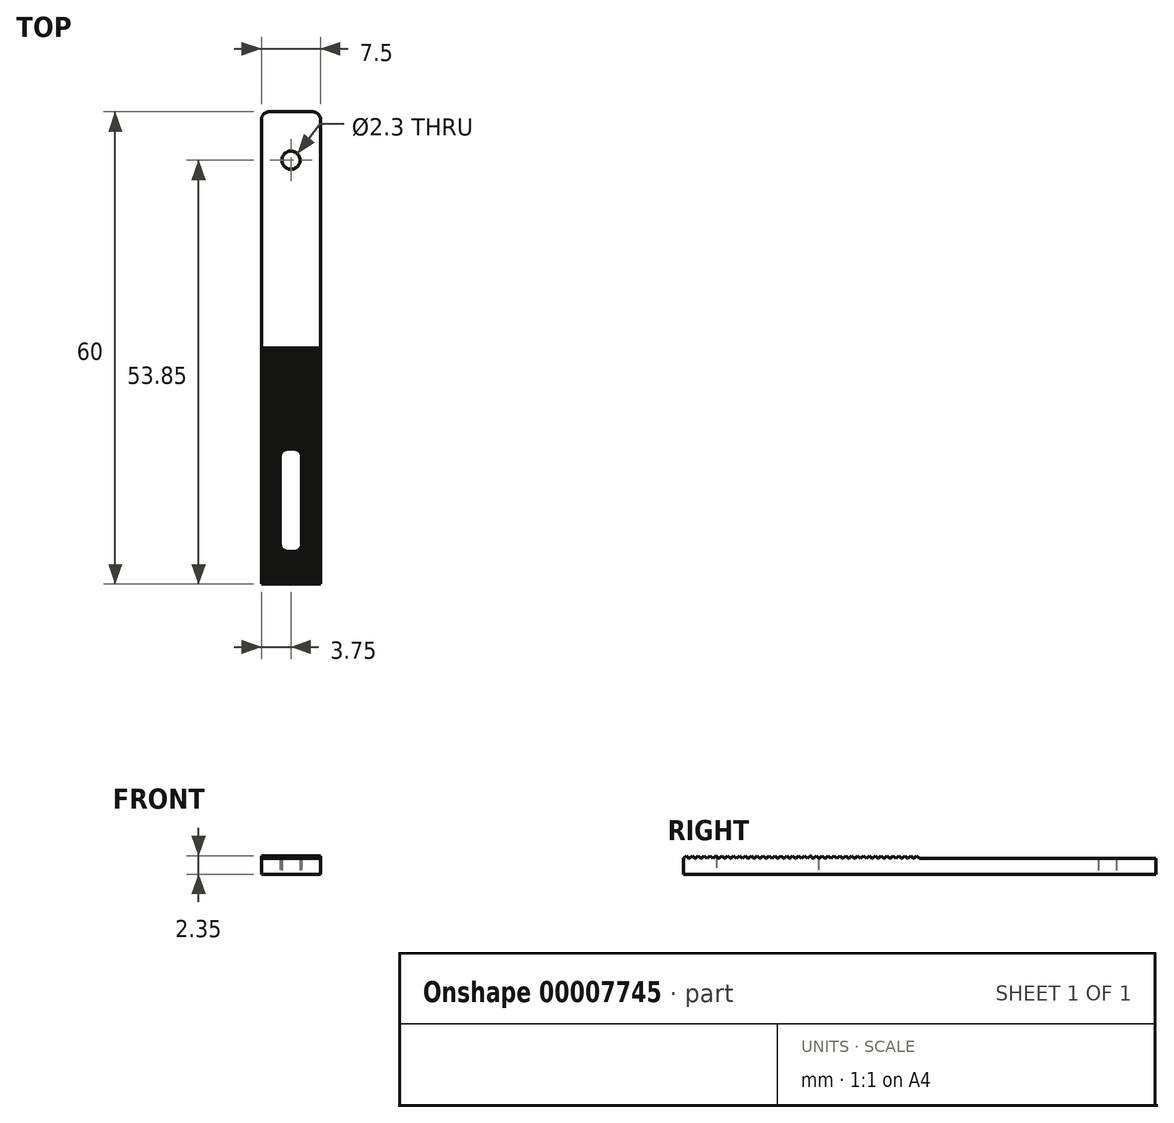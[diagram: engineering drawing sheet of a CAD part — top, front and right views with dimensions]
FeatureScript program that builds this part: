
annotation { "Feature Type Name" : "Feature", "Feature Type Description" : "" }
export const myFeature = defineFeature(function(context is Context, id is Id, definition is map)
    precondition{}
    {
        {
            var Q0;
            Q0=qCreatedBy(makeId("Top.planeOp"),FACE);
            var sketch = newSketch(context, id + "F0", { "sketchPlane" : qUnion([Q0])});
            skLineSegment(sketch, "E0.rect.bottom", {"start": v(6.5, 60) * mm, "end": v(1, 60) * mm});
            skLineSegment(sketch, "E0.rect.top", {"start": v(7.5, 0) * mm, "end": v(0, 0) * mm});
            skLineSegment(sketch, "E0.rect.left", {"start": v(7.5, 59) * mm, "end": v(7.5, 0) * mm});
            skLineSegment(sketch, "E0.rect.right", {"start": v(0, 59) * mm, "end": v(0, 0) * mm});
            skPoint(sketch, "E0.rect.middle", {"position": v(0, 0) * mm});
            skLineSegment(sketch, "E1", {"start": v(3.75, 0) * mm, "end": v(3.75, 4.15) * mm, "construction": true});
            skLineSegment(sketch, "E2.bottom", {"start": v(3.38, 4.15) * mm, "end": v(4.12, 4.15) * mm});
            skLineSegment(sketch, "E2.top", {"start": v(3.37, 17.15) * mm, "end": v(4.12, 17.15) * mm});
            skLineSegment(sketch, "E2.left", {"start": v(2.38, 5.15) * mm, "end": v(2.38, 16.15) * mm});
            skLineSegment(sketch, "E2.right", {"start": v(5.12, 5.15) * mm, "end": v(5.12, 16.15) * mm});
            skPoint(sketch, "E3.visualSharp", {"position": v(2.38, 17.15) * mm});
            skArc(sketch, "E3.filletArc", {"start": v(3.37, 17.15) * mm, "mid": v(2.67, 16.86) * mm, "end": v(2.37, 16.15) * mm});
            skPoint(sketch, "E4.visualSharp", {"position": v(5.12, 17.15) * mm});
            skArc(sketch, "E4.filletArc", {"start": v(5.12, 16.15) * mm, "mid": v(4.83, 16.86) * mm, "end": v(4.12, 17.15) * mm});
            skPoint(sketch, "E5.visualSharp", {"position": v(2.38, 4.15) * mm});
            skArc(sketch, "E5.filletArc", {"start": v(2.38, 5.15) * mm, "mid": v(2.67, 4.44) * mm, "end": v(3.38, 4.15) * mm});
            skPoint(sketch, "E6.visualSharp", {"position": v(5.12, 4.15) * mm});
            skArc(sketch, "E6.filletArc", {"start": v(4.12, 4.15) * mm, "mid": v(4.83, 4.44) * mm, "end": v(5.12, 5.15) * mm});
            skPoint(sketch, "E7.visualSharp", {"position": v(0, 60) * mm});
            skArc(sketch, "E7.filletArc", {"start": v(1, 60) * mm, "mid": v(0.3, 59.7) * mm, "end": v(0, 59) * mm});
            skPoint(sketch, "E8.visualSharp", {"position": v(7.5, 60) * mm});
            skArc(sketch, "E8.filletArc", {"start": v(7.5, 59) * mm, "mid": v(7.2, 59.7) * mm, "end": v(6.5, 60) * mm});
            skPoint(sketch, "E9", {"position": v(3.75, 60) * mm});
            skCircle(sketch, "E10", {"center": v(3.75, 53.85) * mm, "radius": 1.15 * mm});
            skLineSegment(sketch, "E11", {"start": v(3.75, 55) * mm, "end": v(3.75, 60) * mm, "construction": true});
            skSolve(sketch);
        }
        {
            var Q0;
            Q0=makeQuery(id+"F0.imprint","IMPRINT",FACE,{"disambiguationData":[TD([[makeQuery(id+"F0.imprint","IMPRINT",EDGE,{"derivedFrom":sQuery(id+"F0.wireOp",EDGE,"E0.rect.bottom")}),1.0]])]});
            extrude(context, id + "F1", {"entities" : qUnion([Q0]), "depth" : 2 * mm});
        }
        {
            var Q0;
            Q0=makeQuery(id+"F1.opExtrude","SWEPT_FACE",FACE,{"disambiguationData":[OSD([sQuery(id+"F0.wireOp",EDGE,"E0.rect.left")])]});
            var sketch = newSketch(context, id + "F2", { "sketchPlane" : qUnion([Q0])});
            skLineSegment(sketch, "E12.0", {"start": v(59, 2) * mm, "end": v(0, 2) * mm});
            skLineSegment(sketch, "E13", {"start": v(0, 2) * mm, "end": v(0.35, 2.35) * mm});
            skLineSegment(sketch, "E14", {"start": v(0.35, 2.35) * mm, "end": v(0.7, 2) * mm});
            skLineSegment(sketch, "E15.1.0.0", {"start": v(0.75, 2) * mm, "end": v(1.1, 2.35) * mm});
            skLineSegment(sketch, "E15.1.0.1", {"start": v(1.1, 2.35) * mm, "end": v(1.46, 2) * mm});
            skLineSegment(sketch, "E15.2.0.0", {"start": v(1.5, 2) * mm, "end": v(1.85, 2.35) * mm});
            skLineSegment(sketch, "E15.2.0.1", {"start": v(1.85, 2.35) * mm, "end": v(2.2, 2) * mm});
            skLineSegment(sketch, "E15.3.0.0", {"start": v(2.25, 2) * mm, "end": v(2.6, 2.35) * mm});
            skLineSegment(sketch, "E15.3.0.1", {"start": v(2.6, 2.35) * mm, "end": v(2.96, 2) * mm});
            skLineSegment(sketch, "E15.4.0.0", {"start": v(3, 2) * mm, "end": v(3.35, 2.35) * mm});
            skLineSegment(sketch, "E15.4.0.1", {"start": v(3.35, 2.35) * mm, "end": v(3.7, 2) * mm});
            skLineSegment(sketch, "E15.5.0.0", {"start": v(3.75, 2) * mm, "end": v(4.1, 2.35) * mm});
            skLineSegment(sketch, "E15.5.0.1", {"start": v(4.1, 2.35) * mm, "end": v(4.46, 2) * mm});
            skLineSegment(sketch, "E15.6.0.0", {"start": v(4.5, 2) * mm, "end": v(4.85, 2.35) * mm});
            skLineSegment(sketch, "E15.6.0.1", {"start": v(4.85, 2.35) * mm, "end": v(5.2, 2) * mm});
            skLineSegment(sketch, "E15.7.0.0", {"start": v(5.25, 2) * mm, "end": v(5.6, 2.35) * mm});
            skLineSegment(sketch, "E15.7.0.1", {"start": v(5.6, 2.35) * mm, "end": v(5.96, 2) * mm});
            skLineSegment(sketch, "E15.8.0.0", {"start": v(6, 2) * mm, "end": v(6.35, 2.35) * mm});
            skLineSegment(sketch, "E15.8.0.1", {"start": v(6.35, 2.35) * mm, "end": v(6.7, 2) * mm});
            skLineSegment(sketch, "E15.9.0.0", {"start": v(6.75, 2) * mm, "end": v(7.1, 2.35) * mm});
            skLineSegment(sketch, "E15.9.0.1", {"start": v(7.1, 2.35) * mm, "end": v(7.46, 2) * mm});
            skLineSegment(sketch, "E15.10.0.0", {"start": v(7.5, 2) * mm, "end": v(7.85, 2.35) * mm});
            skLineSegment(sketch, "E15.10.0.1", {"start": v(7.85, 2.35) * mm, "end": v(8.2, 2) * mm});
            skLineSegment(sketch, "E15.11.0.0", {"start": v(8.25, 2) * mm, "end": v(8.6, 2.35) * mm});
            skLineSegment(sketch, "E15.11.0.1", {"start": v(8.6, 2.35) * mm, "end": v(8.96, 2) * mm});
            skLineSegment(sketch, "E15.12.0.0", {"start": v(9, 2) * mm, "end": v(9.35, 2.35) * mm});
            skLineSegment(sketch, "E15.12.0.1", {"start": v(9.35, 2.35) * mm, "end": v(9.7, 2) * mm});
            skLineSegment(sketch, "E15.13.0.0", {"start": v(9.75, 2) * mm, "end": v(10.1, 2.35) * mm});
            skLineSegment(sketch, "E15.13.0.1", {"start": v(10.1, 2.35) * mm, "end": v(10.46, 2) * mm});
            skLineSegment(sketch, "E15.14.0.0", {"start": v(10.5, 2) * mm, "end": v(10.85, 2.35) * mm});
            skLineSegment(sketch, "E15.14.0.1", {"start": v(10.85, 2.35) * mm, "end": v(11.2, 2) * mm});
            skLineSegment(sketch, "E15.15.0.0", {"start": v(11.25, 2) * mm, "end": v(11.6, 2.35) * mm});
            skLineSegment(sketch, "E15.15.0.1", {"start": v(11.6, 2.35) * mm, "end": v(11.96, 2) * mm});
            skLineSegment(sketch, "E15.16.0.0", {"start": v(12, 2) * mm, "end": v(12.35, 2.35) * mm});
            skLineSegment(sketch, "E15.16.0.1", {"start": v(12.35, 2.35) * mm, "end": v(12.7, 2) * mm});
            skLineSegment(sketch, "E15.17.0.0", {"start": v(12.75, 2) * mm, "end": v(13.1, 2.35) * mm});
            skLineSegment(sketch, "E15.17.0.1", {"start": v(13.1, 2.35) * mm, "end": v(13.46, 2) * mm});
            skLineSegment(sketch, "E15.18.0.0", {"start": v(13.5, 2) * mm, "end": v(13.85, 2.35) * mm});
            skLineSegment(sketch, "E15.18.0.1", {"start": v(13.85, 2.35) * mm, "end": v(14.2, 2) * mm});
            skLineSegment(sketch, "E15.19.0.0", {"start": v(14.25, 2) * mm, "end": v(14.6, 2.35) * mm});
            skLineSegment(sketch, "E15.19.0.1", {"start": v(14.6, 2.35) * mm, "end": v(14.96, 2) * mm});
            skLineSegment(sketch, "E15.20.0.0", {"start": v(15, 2) * mm, "end": v(15.35, 2.35) * mm});
            skLineSegment(sketch, "E15.20.0.1", {"start": v(15.35, 2.35) * mm, "end": v(15.7, 2) * mm});
            skLineSegment(sketch, "E15.21.0.0", {"start": v(15.75, 2) * mm, "end": v(16.1, 2.35) * mm});
            skLineSegment(sketch, "E15.21.0.1", {"start": v(16.1, 2.35) * mm, "end": v(16.46, 2) * mm});
            skLineSegment(sketch, "E15.22.0.0", {"start": v(16.5, 2) * mm, "end": v(16.85, 2.35) * mm});
            skLineSegment(sketch, "E15.22.0.1", {"start": v(16.85, 2.35) * mm, "end": v(17.2, 2) * mm});
            skLineSegment(sketch, "E15.23.0.0", {"start": v(17.25, 2) * mm, "end": v(17.6, 2.35) * mm});
            skLineSegment(sketch, "E15.23.0.1", {"start": v(17.6, 2.35) * mm, "end": v(17.96, 2) * mm});
            skLineSegment(sketch, "E15.24.0.0", {"start": v(18, 2) * mm, "end": v(18.35, 2.35) * mm});
            skLineSegment(sketch, "E15.24.0.1", {"start": v(18.35, 2.35) * mm, "end": v(18.7, 2) * mm});
            skLineSegment(sketch, "E15.25.0.0", {"start": v(18.75, 2) * mm, "end": v(19.1, 2.35) * mm});
            skLineSegment(sketch, "E15.25.0.1", {"start": v(19.1, 2.35) * mm, "end": v(19.46, 2) * mm});
            skLineSegment(sketch, "E15.26.0.0", {"start": v(19.5, 2) * mm, "end": v(19.85, 2.35) * mm});
            skLineSegment(sketch, "E15.26.0.1", {"start": v(19.85, 2.35) * mm, "end": v(20.2, 2) * mm});
            skLineSegment(sketch, "E15.27.0.0", {"start": v(20.25, 2) * mm, "end": v(20.6, 2.35) * mm});
            skLineSegment(sketch, "E15.27.0.1", {"start": v(20.6, 2.35) * mm, "end": v(20.96, 2) * mm});
            skLineSegment(sketch, "E15.28.0.0", {"start": v(21, 2) * mm, "end": v(21.35, 2.35) * mm});
            skLineSegment(sketch, "E15.28.0.1", {"start": v(21.35, 2.35) * mm, "end": v(21.7, 2) * mm});
            skLineSegment(sketch, "E15.29.0.0", {"start": v(21.75, 2) * mm, "end": v(22.1, 2.35) * mm});
            skLineSegment(sketch, "E15.29.0.1", {"start": v(22.1, 2.35) * mm, "end": v(22.46, 2) * mm});
            skLineSegment(sketch, "E15.30.0.0", {"start": v(22.5, 2) * mm, "end": v(22.85, 2.35) * mm});
            skLineSegment(sketch, "E15.30.0.1", {"start": v(22.85, 2.35) * mm, "end": v(23.2, 2) * mm});
            skLineSegment(sketch, "E15.31.0.0", {"start": v(23.25, 2) * mm, "end": v(23.6, 2.35) * mm});
            skLineSegment(sketch, "E15.31.0.1", {"start": v(23.6, 2.35) * mm, "end": v(23.96, 2) * mm});
            skLineSegment(sketch, "E15.32.0.0", {"start": v(24, 2) * mm, "end": v(24.35, 2.35) * mm});
            skLineSegment(sketch, "E15.32.0.1", {"start": v(24.35, 2.35) * mm, "end": v(24.7, 2) * mm});
            skLineSegment(sketch, "E15.33.0.0", {"start": v(24.75, 2) * mm, "end": v(25.1, 2.35) * mm});
            skLineSegment(sketch, "E15.33.0.1", {"start": v(25.1, 2.35) * mm, "end": v(25.46, 2) * mm});
            skLineSegment(sketch, "E15.direction1", {"start": v(0, 2) * mm, "end": v(0.75, 2) * mm, "construction": true});
            skLineSegment(sketch, "E16.0.34.0", {"start": v(25.5, 2) * mm, "end": v(25.85, 2.35) * mm});
            skLineSegment(sketch, "E16.3.34.0", {"start": v(25.85, 2.35) * mm, "end": v(26.2, 2) * mm});
            skLineSegment(sketch, "E16.0.35.0", {"start": v(26.25, 2) * mm, "end": v(26.6, 2.35) * mm});
            skLineSegment(sketch, "E16.3.35.0", {"start": v(26.6, 2.35) * mm, "end": v(26.96, 2) * mm});
            skLineSegment(sketch, "E16.0.36.0", {"start": v(27, 2) * mm, "end": v(27.35, 2.35) * mm});
            skLineSegment(sketch, "E16.3.36.0", {"start": v(27.35, 2.35) * mm, "end": v(27.7, 2) * mm});
            skLineSegment(sketch, "E16.0.37.0", {"start": v(27.75, 2) * mm, "end": v(28.1, 2.35) * mm});
            skLineSegment(sketch, "E16.3.37.0", {"start": v(28.1, 2.35) * mm, "end": v(28.46, 2) * mm});
            skLineSegment(sketch, "E16.0.38.0", {"start": v(28.5, 2) * mm, "end": v(28.85, 2.35) * mm});
            skLineSegment(sketch, "E16.3.38.0", {"start": v(28.85, 2.35) * mm, "end": v(29.2, 2) * mm});
            skLineSegment(sketch, "E16.0.39.0", {"start": v(29.25, 2) * mm, "end": v(29.6, 2.35) * mm});
            skLineSegment(sketch, "E16.3.39.0", {"start": v(29.6, 2.35) * mm, "end": v(29.96, 2) * mm});
            skSolve(sketch);
        }
        {
            var Q0;
            {var subQ1=sQuery(id+"F2.wireOp",EDGE,"E16.0.39.0");Q0=makeQuery(id+"F2.imprint","IMPRINT",FACE,{"disambiguationData":[TD([[makeQuery(id+"F2.imprint","IMPRINT",EDGE,{"derivedFrom":subQ1}),-1.0]])]});}
            var Q1;
            {var subQ1=sQuery(id+"F2.wireOp",EDGE,"E16.0.38.0");Q1=makeQuery(id+"F2.imprint","IMPRINT",FACE,{"disambiguationData":[TD([[makeQuery(id+"F2.imprint","IMPRINT",EDGE,{"derivedFrom":subQ1}),-1.0]])]});}
            var Q2;
            {var subQ1=sQuery(id+"F2.wireOp",EDGE,"E16.0.37.0");Q2=makeQuery(id+"F2.imprint","IMPRINT",FACE,{"disambiguationData":[TD([[makeQuery(id+"F2.imprint","IMPRINT",EDGE,{"derivedFrom":subQ1}),-1.0]])]});}
            var Q3;
            {var subQ1=sQuery(id+"F2.wireOp",EDGE,"E16.0.36.0");Q3=makeQuery(id+"F2.imprint","IMPRINT",FACE,{"disambiguationData":[TD([[makeQuery(id+"F2.imprint","IMPRINT",EDGE,{"derivedFrom":subQ1}),-1.0]])]});}
            var Q4;
            {var subQ1=sQuery(id+"F2.wireOp",EDGE,"E16.0.35.0");Q4=makeQuery(id+"F2.imprint","IMPRINT",FACE,{"disambiguationData":[TD([[makeQuery(id+"F2.imprint","IMPRINT",EDGE,{"derivedFrom":subQ1}),-1.0]])]});}
            var Q5;
            {var subQ1=sQuery(id+"F2.wireOp",EDGE,"E16.0.34.0");Q5=makeQuery(id+"F2.imprint","IMPRINT",FACE,{"disambiguationData":[TD([[makeQuery(id+"F2.imprint","IMPRINT",EDGE,{"derivedFrom":subQ1}),-1.0]])]});}
            var Q6;
            {var subQ1=sQuery(id+"F2.wireOp",EDGE,"E15.33.0.0");Q6=makeQuery(id+"F2.imprint","IMPRINT",FACE,{"disambiguationData":[TD([[makeQuery(id+"F2.imprint","IMPRINT",EDGE,{"derivedFrom":subQ1}),-1.0]])]});}
            var Q7;
            {var subQ1=sQuery(id+"F2.wireOp",EDGE,"E15.32.0.0");Q7=makeQuery(id+"F2.imprint","IMPRINT",FACE,{"disambiguationData":[TD([[makeQuery(id+"F2.imprint","IMPRINT",EDGE,{"derivedFrom":subQ1}),-1.0]])]});}
            var Q8;
            {var subQ1=sQuery(id+"F2.wireOp",EDGE,"E15.31.0.0");Q8=makeQuery(id+"F2.imprint","IMPRINT",FACE,{"disambiguationData":[TD([[makeQuery(id+"F2.imprint","IMPRINT",EDGE,{"derivedFrom":subQ1}),-1.0]])]});}
            var Q9;
            {var subQ1=sQuery(id+"F2.wireOp",EDGE,"E15.30.0.0");Q9=makeQuery(id+"F2.imprint","IMPRINT",FACE,{"disambiguationData":[TD([[makeQuery(id+"F2.imprint","IMPRINT",EDGE,{"derivedFrom":subQ1}),-1.0]])]});}
            var Q10;
            {var subQ1=sQuery(id+"F2.wireOp",EDGE,"E15.29.0.0");Q10=makeQuery(id+"F2.imprint","IMPRINT",FACE,{"disambiguationData":[TD([[makeQuery(id+"F2.imprint","IMPRINT",EDGE,{"derivedFrom":subQ1}),-1.0]])]});}
            var Q11;
            {var subQ1=sQuery(id+"F2.wireOp",EDGE,"E15.28.0.0");Q11=makeQuery(id+"F2.imprint","IMPRINT",FACE,{"disambiguationData":[TD([[makeQuery(id+"F2.imprint","IMPRINT",EDGE,{"derivedFrom":subQ1}),-1.0]])]});}
            var Q12;
            {var subQ1=sQuery(id+"F2.wireOp",EDGE,"E15.27.0.0");Q12=makeQuery(id+"F2.imprint","IMPRINT",FACE,{"disambiguationData":[TD([[makeQuery(id+"F2.imprint","IMPRINT",EDGE,{"derivedFrom":subQ1}),-1.0]])]});}
            var Q13;
            {var subQ1=sQuery(id+"F2.wireOp",EDGE,"E15.26.0.0");Q13=makeQuery(id+"F2.imprint","IMPRINT",FACE,{"disambiguationData":[TD([[makeQuery(id+"F2.imprint","IMPRINT",EDGE,{"derivedFrom":subQ1}),-1.0]])]});}
            var Q14;
            {var subQ1=sQuery(id+"F2.wireOp",EDGE,"E15.25.0.0");Q14=makeQuery(id+"F2.imprint","IMPRINT",FACE,{"disambiguationData":[TD([[makeQuery(id+"F2.imprint","IMPRINT",EDGE,{"derivedFrom":subQ1}),-1.0]])]});}
            var Q15;
            {var subQ1=sQuery(id+"F2.wireOp",EDGE,"E15.24.0.0");Q15=makeQuery(id+"F2.imprint","IMPRINT",FACE,{"disambiguationData":[TD([[makeQuery(id+"F2.imprint","IMPRINT",EDGE,{"derivedFrom":subQ1}),-1.0]])]});}
            var Q16;
            {var subQ1=sQuery(id+"F2.wireOp",EDGE,"E15.23.0.0");Q16=makeQuery(id+"F2.imprint","IMPRINT",FACE,{"disambiguationData":[TD([[makeQuery(id+"F2.imprint","IMPRINT",EDGE,{"derivedFrom":subQ1}),-1.0]])]});}
            var Q17;
            {var subQ1=sQuery(id+"F2.wireOp",EDGE,"E15.22.0.0");Q17=makeQuery(id+"F2.imprint","IMPRINT",FACE,{"disambiguationData":[TD([[makeQuery(id+"F2.imprint","IMPRINT",EDGE,{"derivedFrom":subQ1}),-1.0]])]});}
            var Q18;
            {var subQ1=sQuery(id+"F2.wireOp",EDGE,"E15.21.0.0");Q18=makeQuery(id+"F2.imprint","IMPRINT",FACE,{"disambiguationData":[TD([[makeQuery(id+"F2.imprint","IMPRINT",EDGE,{"derivedFrom":subQ1}),-1.0]])]});}
            var Q19;
            {var subQ1=sQuery(id+"F2.wireOp",EDGE,"E15.20.0.0");Q19=makeQuery(id+"F2.imprint","IMPRINT",FACE,{"disambiguationData":[TD([[makeQuery(id+"F2.imprint","IMPRINT",EDGE,{"derivedFrom":subQ1}),-1.0]])]});}
            var Q20;
            {var subQ1=sQuery(id+"F2.wireOp",EDGE,"E15.19.0.0");Q20=makeQuery(id+"F2.imprint","IMPRINT",FACE,{"disambiguationData":[TD([[makeQuery(id+"F2.imprint","IMPRINT",EDGE,{"derivedFrom":subQ1}),-1.0]])]});}
            var Q21;
            {var subQ1=sQuery(id+"F2.wireOp",EDGE,"E15.18.0.0");Q21=makeQuery(id+"F2.imprint","IMPRINT",FACE,{"disambiguationData":[TD([[makeQuery(id+"F2.imprint","IMPRINT",EDGE,{"derivedFrom":subQ1}),-1.0]])]});}
            var Q22;
            {var subQ1=sQuery(id+"F2.wireOp",EDGE,"E15.17.0.0");Q22=makeQuery(id+"F2.imprint","IMPRINT",FACE,{"disambiguationData":[TD([[makeQuery(id+"F2.imprint","IMPRINT",EDGE,{"derivedFrom":subQ1}),-1.0]])]});}
            var Q23;
            {var subQ1=sQuery(id+"F2.wireOp",EDGE,"E15.16.0.0");Q23=makeQuery(id+"F2.imprint","IMPRINT",FACE,{"disambiguationData":[TD([[makeQuery(id+"F2.imprint","IMPRINT",EDGE,{"derivedFrom":subQ1}),-1.0]])]});}
            var Q24;
            {var subQ1=sQuery(id+"F2.wireOp",EDGE,"E15.15.0.0");Q24=makeQuery(id+"F2.imprint","IMPRINT",FACE,{"disambiguationData":[TD([[makeQuery(id+"F2.imprint","IMPRINT",EDGE,{"derivedFrom":subQ1}),-1.0]])]});}
            var Q25;
            {var subQ1=sQuery(id+"F2.wireOp",EDGE,"E15.14.0.0");Q25=makeQuery(id+"F2.imprint","IMPRINT",FACE,{"disambiguationData":[TD([[makeQuery(id+"F2.imprint","IMPRINT",EDGE,{"derivedFrom":subQ1}),-1.0]])]});}
            var Q26;
            {var subQ1=sQuery(id+"F2.wireOp",EDGE,"E15.13.0.0");Q26=makeQuery(id+"F2.imprint","IMPRINT",FACE,{"disambiguationData":[TD([[makeQuery(id+"F2.imprint","IMPRINT",EDGE,{"derivedFrom":subQ1}),-1.0]])]});}
            var Q27;
            {var subQ1=sQuery(id+"F2.wireOp",EDGE,"E15.12.0.0");Q27=makeQuery(id+"F2.imprint","IMPRINT",FACE,{"disambiguationData":[TD([[makeQuery(id+"F2.imprint","IMPRINT",EDGE,{"derivedFrom":subQ1}),-1.0]])]});}
            var Q28;
            {var subQ1=sQuery(id+"F2.wireOp",EDGE,"E15.11.0.0");Q28=makeQuery(id+"F2.imprint","IMPRINT",FACE,{"disambiguationData":[TD([[makeQuery(id+"F2.imprint","IMPRINT",EDGE,{"derivedFrom":subQ1}),-1.0]])]});}
            var Q29;
            {var subQ0=sQuery(id+"F2.wireOp",EDGE,"E15.10.0.0");Q29=makeQuery(id+"F2.imprint","IMPRINT",FACE,{"disambiguationData":[TD([[makeQuery(id+"F2.imprint","IMPRINT",EDGE,{"derivedFrom":subQ0}),-1.0]])]});}
            var Q30;
            {var subQ1=sQuery(id+"F2.wireOp",EDGE,"E15.9.0.0");Q30=makeQuery(id+"F2.imprint","IMPRINT",FACE,{"disambiguationData":[TD([[makeQuery(id+"F2.imprint","IMPRINT",EDGE,{"derivedFrom":subQ1}),-1.0]])]});}
            var Q31;
            {var subQ1=sQuery(id+"F2.wireOp",EDGE,"E15.8.0.0");Q31=makeQuery(id+"F2.imprint","IMPRINT",FACE,{"disambiguationData":[TD([[makeQuery(id+"F2.imprint","IMPRINT",EDGE,{"derivedFrom":subQ1}),-1.0]])]});}
            var Q32;
            {var subQ1=sQuery(id+"F2.wireOp",EDGE,"E15.7.0.0");Q32=makeQuery(id+"F2.imprint","IMPRINT",FACE,{"disambiguationData":[TD([[makeQuery(id+"F2.imprint","IMPRINT",EDGE,{"derivedFrom":subQ1}),-1.0]])]});}
            var Q33;
            {var subQ1=sQuery(id+"F2.wireOp",EDGE,"E15.6.0.0");Q33=makeQuery(id+"F2.imprint","IMPRINT",FACE,{"disambiguationData":[TD([[makeQuery(id+"F2.imprint","IMPRINT",EDGE,{"derivedFrom":subQ1}),-1.0]])]});}
            var Q34;
            {var subQ1=sQuery(id+"F2.wireOp",EDGE,"E15.5.0.0");Q34=makeQuery(id+"F2.imprint","IMPRINT",FACE,{"disambiguationData":[TD([[makeQuery(id+"F2.imprint","IMPRINT",EDGE,{"derivedFrom":subQ1}),-1.0]])]});}
            var Q35;
            {var subQ1=sQuery(id+"F2.wireOp",EDGE,"E15.4.0.0");Q35=makeQuery(id+"F2.imprint","IMPRINT",FACE,{"disambiguationData":[TD([[makeQuery(id+"F2.imprint","IMPRINT",EDGE,{"derivedFrom":subQ1}),-1.0]])]});}
            var Q36;
            {var subQ1=sQuery(id+"F2.wireOp",EDGE,"E15.3.0.0");Q36=makeQuery(id+"F2.imprint","IMPRINT",FACE,{"disambiguationData":[TD([[makeQuery(id+"F2.imprint","IMPRINT",EDGE,{"derivedFrom":subQ1}),-1.0]])]});}
            var Q37;
            {var subQ1=sQuery(id+"F2.wireOp",EDGE,"E15.2.0.0");Q37=makeQuery(id+"F2.imprint","IMPRINT",FACE,{"disambiguationData":[TD([[makeQuery(id+"F2.imprint","IMPRINT",EDGE,{"derivedFrom":subQ1}),-1.0]])]});}
            var Q38;
            {var subQ1=sQuery(id+"F2.wireOp",EDGE,"E15.1.0.0");Q38=makeQuery(id+"F2.imprint","IMPRINT",FACE,{"disambiguationData":[TD([[makeQuery(id+"F2.imprint","IMPRINT",EDGE,{"derivedFrom":subQ1}),-1.0]])]});}
            var Q39;
            {var subQ1=sQuery(id+"F2.wireOp",EDGE,"E13");Q39=makeQuery(id+"F2.imprint","IMPRINT",FACE,{"disambiguationData":[TD([[makeQuery(id+"F2.imprint","IMPRINT",EDGE,{"derivedFrom":subQ1}),-1.0]])]});}
            var Q40;
            Q40=makeQuery(id+"F1.opExtrude","SWEPT_FACE",FACE,{"disambiguationData":[OSD([sQuery(id+"F0.wireOp",EDGE,"E0.rect.right")])]});
            extrude(context, id + "F3", {"entities" : qUnion([Q0, Q1, Q2, Q3, Q4, Q5, Q6, Q7, Q8, Q9, Q10, Q11, Q12, Q13, Q14, Q15, Q16, Q17, Q18, Q19, Q20, Q21, Q22, Q23, Q24, Q25, Q26, Q27, Q28, Q29, Q30, Q31, Q32, Q33, Q34, Q35, Q36, Q37, Q38, Q39]), "operationType" : NewBodyOperationType.ADD, "endBound" : BoundingType.UP_TO_SURFACE, "oppositeDirection" : true, "endBoundEntityFace" : qUnion([Q40]), "depth" : 25 * mm});
        }
        {
            var Q0;
            Q0=makeQuery(id+"F0.imprint","IMPRINT",FACE,{"disambiguationData":[TD([[makeQuery(id+"F0.imprint","IMPRINT",EDGE,{"derivedFrom":sQuery(id+"F0.wireOp",EDGE,"E2.bottom")}),1.0]])]});
            extrude(context, id + "F4", {"entities" : qUnion([Q0]), "operationType" : NewBodyOperationType.REMOVE, "endBound" : BoundingType.THROUGH_ALL, "depth" : 25 * mm});
        }
    });
